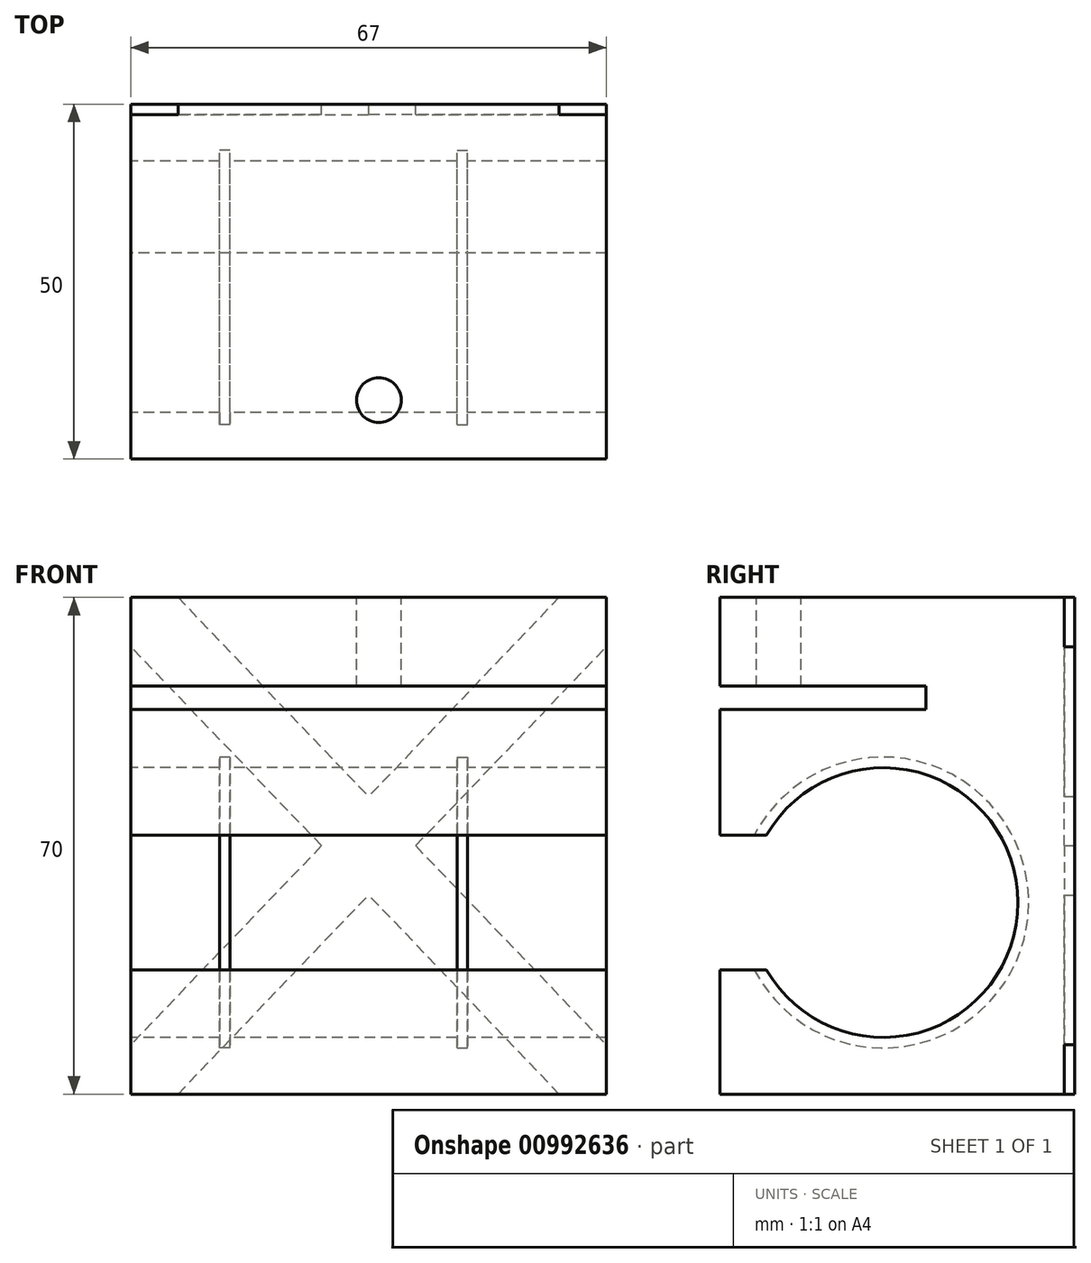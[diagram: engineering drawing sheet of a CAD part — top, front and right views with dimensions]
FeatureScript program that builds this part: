
annotation { "Feature Type Name" : "Feature", "Feature Type Description" : "" }
export const myFeature = defineFeature(function(context is Context, id is Id, definition is map)
    precondition{}
    {
        {
            var Q0;
            Q0=qCreatedBy(makeId("Front.planeOp"),FACE);
            var sketch = newSketch(context, id + "F0", { "sketchPlane" : qUnion([Q0])});
            skLineSegment(sketch, "E0", {"start": v(-34.95, 35.36) * mm, "end": v(-34.95, -34.64) * mm});
            skLineSegment(sketch, "E1", {"start": v(-34.95, -34.64) * mm, "end": v(32.05, -34.64) * mm});
            skLineSegment(sketch, "E2", {"start": v(32.05, -34.64) * mm, "end": v(32.05, 35.36) * mm});
            skLineSegment(sketch, "E3", {"start": v(32.05, 35.36) * mm, "end": v(-34.95, 35.36) * mm});
            skSolve(sketch);
        }
        {
            var Q0;
            Q0=makeQuery(id+"F0.imprint","IMPRINT",FACE,{"disambiguationData":[TD([[makeQuery(id+"F0.imprint","IMPRINT",EDGE,{"derivedFrom":sQuery(id+"F0.wireOp",EDGE,"E0")}),1.0]])]});
            extrude(context, id + "F1", {"entities" : qUnion([Q0]), "depth" : 50 * mm, "offsetDistance" : 25 * mm});
        }
        {
            var Q0;
            Q0=makeQuery(id+"F1.opExtrude","CAP_FACE",FACE,{"disambiguationData":[OSD([sQuery(id+"F0.wireOp",EDGE,"E0"),sQuery(id+"F0.wireOp",EDGE,"E1"),sQuery(id+"F0.wireOp",EDGE,"E2"),sQuery(id+"F0.wireOp",EDGE,"E3")])],"isStart":true});
            var sketch = newSketch(context, id + "F2", { "sketchPlane" : qUnion([Q0])});
            skLineSegment(sketch, "E4", {"start": v(-32.05, -34.64) * mm, "end": v(34.95, 35.36) * mm});
            skLineSegment(sketch, "E5", {"start": v(34.95, -34.64) * mm, "end": v(-32.05, 35.36) * mm});
            skLineSegment(sketch, "E6", {"start": v(-32.05, 35.36) * mm, "end": v(-25.41, 35.36) * mm});
            skLineSegment(sketch, "E7", {"start": v(-25.41, 35.36) * mm, "end": v(34.95, -27.7) * mm});
            skLineSegment(sketch, "E8", {"start": v(34.95, -27.7) * mm, "end": v(34.95, -34.64) * mm});
            skLineSegment(sketch, "E9", {"start": v(28.3, -34.64) * mm, "end": v(-32.05, 28.41) * mm});
            skLineSegment(sketch, "E10", {"start": v(-32.05, 28.41) * mm, "end": v(-32.05, 35.36) * mm});
            skLineSegment(sketch, "E11", {"start": v(-32.05, -34.64) * mm, "end": v(-25.41, -34.64) * mm});
            skLineSegment(sketch, "E12", {"start": v(-25.41, -34.64) * mm, "end": v(34.95, 28.41) * mm});
            skLineSegment(sketch, "E13", {"start": v(34.95, 28.41) * mm, "end": v(34.95, 35.36) * mm});
            skLineSegment(sketch, "E14", {"start": v(28.3, 35.36) * mm, "end": v(-32.05, -27.7) * mm});
            skLineSegment(sketch, "E15", {"start": v(-32.05, -27.7) * mm, "end": v(-32.05, -34.64) * mm});
            skSolve(sketch);
        }
        {
            var Q0;
            Q0=qSketchRegion(id+"F2",true);
            var Q1;
            {var subQ0=sQuery(id+"F2.wireOp",EDGE,"E4");var subQ3=sQuery(id+"F2.wireOp",EDGE,"E7");var subQ4=makeQuery(id+"F2.imprint","INTERSECT",VERTEX,{"derivedFrom":[subQ0,subQ3]});Q1=makeQuery(id+"F2.imprint","IMPRINT",FACE,{"disambiguationData":[TD([[makeQuery(id+"F2.imprint","IMPRINT",EDGE,{"disambiguationData":[TD([[subQ4,1.0]])],"derivedFrom":subQ3}),1.0]])]});}
            var Q2;
            {var subQ1=makeQuery(id+"F1.opExtrude","CAP_EDGE",EDGE,{"disambiguationData":[OSD([sQuery(id+"F0.wireOp",EDGE,"E1")])],"isStart":true});var subQ5=sQuery(id+"F2.wireOp",EDGE,"E9");var subQ6=makeQuery(id+"F2.imprint","INTERSECT",VERTEX,{"derivedFrom":[subQ1,subQ5]});Q2=makeQuery(id+"F2.imprint","IMPRINT",FACE,{"disambiguationData":[TD([[makeQuery(id+"F2.imprint","IMPRINT",EDGE,{"disambiguationData":[TD([[subQ6,-1.0]])],"derivedFrom":subQ5}),-1.0]])]});}
            extrude(context, id + "F3", {"entities" : qUnion([Q0, Q1, Q2]), "operationType" : NewBodyOperationType.REMOVE, "oppositeDirection" : true, "depth" : 1.5 * mm, "offsetDistance" : 25 * mm});
        }
        {
            var Q0;
            Q0=makeQuery(id+"F1.opExtrude","SWEPT_FACE",FACE,{"disambiguationData":[OSD([sQuery(id+"F0.wireOp",EDGE,"E0")])]});
            var sketch = newSketch(context, id + "F4", { "sketchPlane" : qUnion([Q0])});
            skCircle(sketch, "E16", {"center": v(27, -7.64) * mm, "radius": 19 * mm});
            skLineSegment(sketch, "E17", {"start": v(27, -7.64) * mm, "end": v(50, -7.64) * mm});
            skLineSegment(sketch, "E18", {"start": v(50, -7.64) * mm, "end": v(50, 1.86) * mm});
            skLineSegment(sketch, "E19", {"start": v(50, 1.86) * mm, "end": v(43.45, 1.86) * mm});
            skLineSegment(sketch, "E20", {"start": v(50, -7.64) * mm, "end": v(50, -17.14) * mm});
            skLineSegment(sketch, "E21", {"start": v(50, -17.14) * mm, "end": v(43.45, -17.14) * mm});
            skArc(sketch, "E22", {"start": v(43.45, -17.14) * mm, "mid": v(46.01, -7.64) * mm, "end": v(43.45, 1.86) * mm});
            skSolve(sketch);
        }
        {
            var Q0;
            {var subQ1=sQuery(id+"F4.wireOp",EDGE,"E16");var subQ3=sQuery(id+"F4.wireOp",EDGE,"E17");var subQ4=makeQuery(id+"F4.imprint","INTERSECT",VERTEX,{"derivedFrom":[subQ1,subQ3]});Q0=makeQuery(id+"F4.imprint","IMPRINT",FACE,{"disambiguationData":[TD([[makeQuery(id+"F4.imprint","IMPRINT",EDGE,{"disambiguationData":[TD([[subQ4,-1.0]])],"derivedFrom":subQ3}),1.0]])]});}
            var Q1;
            {var subQ1=sQuery(id+"F4.wireOp",EDGE,"E16");var subQ3=sQuery(id+"F4.wireOp",EDGE,"E17");var subQ4=makeQuery(id+"F4.imprint","INTERSECT",VERTEX,{"derivedFrom":[subQ1,subQ3]});Q1=makeQuery(id+"F4.imprint","IMPRINT",FACE,{"disambiguationData":[TD([[makeQuery(id+"F4.imprint","IMPRINT",EDGE,{"disambiguationData":[TD([[subQ4,-1.0]])],"derivedFrom":subQ3}),-1.0]])]});}
            var Q2;
            {var subQ0=sQuery(id+"F4.wireOp",EDGE,"E18");Q2=makeQuery(id+"F4.imprint","IMPRINT",FACE,{"disambiguationData":[TD([[makeQuery(id+"F4.imprint","IMPRINT",EDGE,{"derivedFrom":subQ0}),-1.0]])]});}
            var Q3;
            {var subQ1=sQuery(id+"F4.wireOp",EDGE,"E16");var subQ3=makeQuery(id+"F4.imprint","INTERSECT",VERTEX,{"derivedFrom":[subQ1,sQuery(id+"F4.wireOp",EDGE,"E17")]});Q3=makeQuery(id+"F4.imprint","IMPRINT",FACE,{"disambiguationData":[TD([[makeQuery(id+"F4.imprint","IMPRINT",EDGE,{"disambiguationData":[TD([[subQ3,-1.0]])],"derivedFrom":subQ1}),1.0]])]});}
            var Q4;
            {var subQ0=sQuery(id+"F4.wireOp",EDGE,"E20");Q4=makeQuery(id+"F4.imprint","IMPRINT",FACE,{"disambiguationData":[TD([[makeQuery(id+"F4.imprint","IMPRINT",EDGE,{"derivedFrom":subQ0}),-1.0]])]});}
            extrude(context, id + "F5", {"entities" : qUnion([Q0, Q1, Q2, Q3, Q4]), "operationType" : NewBodyOperationType.REMOVE, "endBound" : BoundingType.UP_TO_NEXT, "oppositeDirection" : true, "depth" : 25 * mm, "offsetDistance" : 25 * mm});
        }
        {
            var Q0;
            Q0=qCreatedBy(makeId("Right.planeOp"),FACE);
            cPlane(context, id + "F6", {"entities" : qUnion([Q0]), "cplaneType" : CPlaneType.OFFSET, "offset" : 12.5 * mm, "width" : 150 * mm, "height" : 150 * mm});
        }
        {
            var Q0;
            Q0=qCreatedBy(id+"F6.planeOp",FACE);
            var sketch = newSketch(context, id + "F7", { "sketchPlane" : qUnion([Q0])});
            skCircle(sketch, "E23", {"center": v(-27, -7.64) * mm, "radius": 20.5 * mm});
            skSolve(sketch);
        }
        {
            var Q0;
            Q0=makeQuery(id+"F7.imprint","IMPRINT",FACE,{"disambiguationData":[TD([[makeQuery(id+"F7.imprint","IMPRINT",EDGE,{"derivedFrom":sQuery(id+"F7.wireOp",EDGE,"E23")}),1.0]])]});
            extrude(context, id + "F8", {"entities" : qUnion([Q0]), "operationType" : NewBodyOperationType.REMOVE, "oppositeDirection" : true, "depth" : 1.5 * mm, "offsetDistance" : 25 * mm});
        }
        {
            var Q0;
            Q0=makeQuery(id+"F1.opExtrude","SWEPT_FACE",FACE,{"disambiguationData":[OSD([sQuery(id+"F0.wireOp",EDGE,"E0")])]});
            var sketch = newSketch(context, id + "F9", { "sketchPlane" : qUnion([Q0])});
            skLineSegment(sketch, "E24", {"start": v(50, 19.56) * mm, "end": v(21, 19.56) * mm});
            skLineSegment(sketch, "E25", {"start": v(21, 19.56) * mm, "end": v(21, 22.86) * mm});
            skLineSegment(sketch, "E26", {"start": v(21, 22.86) * mm, "end": v(50, 22.86) * mm});
            skLineSegment(sketch, "E27", {"start": v(50, 22.86) * mm, "end": v(50, 19.56) * mm});
            skSolve(sketch);
        }
        {
            var Q0;
            Q0=makeQuery(id+"F9.imprint","IMPRINT",FACE,{"disambiguationData":[TD([[makeQuery(id+"F9.imprint","IMPRINT",EDGE,{"derivedFrom":sQuery(id+"F9.wireOp",EDGE,"E24")}),-1.0]])]});
            extrude(context, id + "F10", {"entities" : qUnion([Q0]), "operationType" : NewBodyOperationType.REMOVE, "endBound" : BoundingType.UP_TO_NEXT, "oppositeDirection" : true, "depth" : 25 * mm, "offsetDistance" : 25 * mm});
        }
        {
            var Q0;
            Q0=makeQuery(id+"F1.opExtrude","SWEPT_FACE",FACE,{"disambiguationData":[OSD([sQuery(id+"F0.wireOp",EDGE,"E0")])]});
            cPlane(context, id + "F11", {"entities" : qUnion([Q0]), "cplaneType" : CPlaneType.OFFSET, "offset" : 12.5 * mm, "oppositeDirection" : true, "width" : 150 * mm, "height" : 150 * mm});
        }
        {
            var Q0;
            Q0=qCreatedBy(id+"F11.planeOp",FACE);
            var sketch = newSketch(context, id + "F12", { "sketchPlane" : qUnion([Q0])});
            skCircle(sketch, "E28", {"center": v(27, -7.64) * mm, "radius": 20.5 * mm});
            skSolve(sketch);
        }
        {
            var Q0;
            Q0=qSketchRegion(id+"F12",true);
            extrude(context, id + "F13", {"entities" : qUnion([Q0]), "operationType" : NewBodyOperationType.REMOVE, "oppositeDirection" : true, "depth" : 1.5 * mm, "offsetDistance" : 25 * mm});
        }
        {
            var Q0;
            Q0=makeQuery(id+"F1.opExtrude","SWEPT_FACE",FACE,{"disambiguationData":[OSD([sQuery(id+"F0.wireOp",EDGE,"E3")])]});
            var sketch = newSketch(context, id + "F14", { "sketchPlane" : qUnion([Q0])});
            skCircle(sketch, "E29", {"center": v(0, -41.7) * mm, "radius": 3.15 * mm});
            skSolve(sketch);
        }
        {
            var Q0;
            Q0=makeQuery(id+"F14.imprint","IMPRINT",FACE,{"disambiguationData":[TD([[makeQuery(id+"F14.imprint","IMPRINT",EDGE,{"derivedFrom":sQuery(id+"F14.wireOp",EDGE,"E29")}),1.0]])]});
            extrude(context, id + "F15", {"entities" : qUnion([Q0]), "operationType" : NewBodyOperationType.REMOVE, "endBound" : BoundingType.UP_TO_NEXT, "oppositeDirection" : true, "depth" : 25 * mm, "offsetDistance" : 25 * mm});
        }
    });
